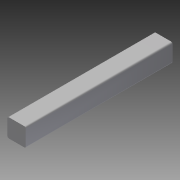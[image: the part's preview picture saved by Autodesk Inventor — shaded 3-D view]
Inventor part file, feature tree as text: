
AUTODESK INVENTOR PART (.ipt)
format: ipt  version: 2013 (Build 170138000, 138)  size: 77,312 bytes
history: native  units: in
note: dims shown in document units (in); Inventor stores cm internally (conversion verified against a paired STEP export)
features: extrude x1, fillet x1, sketch x1
ambient origin geometry x8: Origin, YZ Plane, XZ Plane, XY Plane, X Axis, Y Axis, Z Axis, Center Point
bodies: Solid1 (feature_tree)
feature tree (3):
  extrude  "Extrusion1"  Depth=1.0in TaperAngle=0.0deg
  fillet  "Fillet1"  Radius=0.01in
  sketch  "Sketch1"  dims[d0=0.125in d2=1.0in d3=0.0in d4=0.01in]
